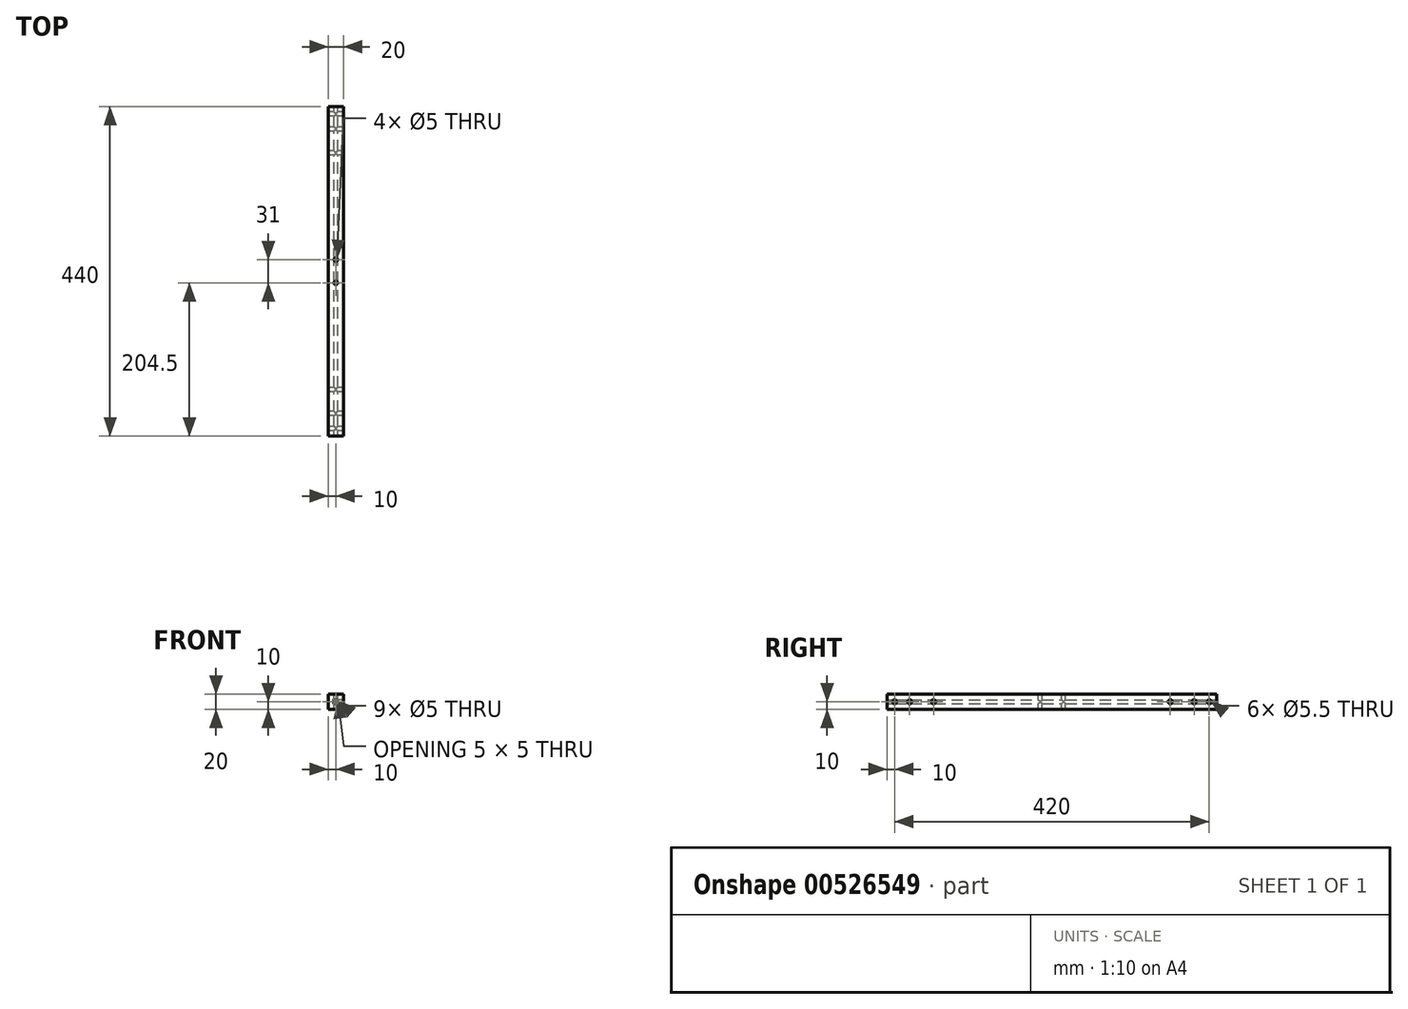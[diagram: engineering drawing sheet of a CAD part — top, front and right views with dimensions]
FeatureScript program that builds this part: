
annotation { "Feature Type Name" : "Feature", "Feature Type Description" : "" }
export const myFeature = defineFeature(function(context is Context, id is Id, definition is map)
    precondition{}
    {
        {
            var Q0;
            Q0=qCreatedBy(makeId("Front.planeOp"),FACE);
            var sketch = newSketch(context, id + "F0", { "sketchPlane" : qUnion([Q0])});
            skLineSegment(sketch, "E0.bottom", {"start": v(-10, 10) * mm, "end": v(10, 10) * mm});
            skLineSegment(sketch, "E0.top", {"start": v(-10, -10) * mm, "end": v(10, -10) * mm});
            skLineSegment(sketch, "E0.left", {"start": v(-10, 10) * mm, "end": v(-10, -10) * mm});
            skLineSegment(sketch, "E0.right", {"start": v(10, 10) * mm, "end": v(10, -10) * mm});
            skPoint(sketch, "E0.middle", {"position": v(0, 0) * mm});
            skCircle(sketch, "E1", {"center": v(0, 0) * mm, "radius": 2.5 * mm});
            skSolve(sketch);
        }
        {
            var Q0;
            Q0 = qSketchRegion(id + "F0", true);
            extrude(context, id + "F1", {"entities" : qUnion([Q0]), "endBound" : BoundingType.SYMMETRIC, "depth" : 440 * mm, "offsetDistance" : 25 * mm});
        }
        {
            var Q0;
            Q0=makeQuery(id+"F1.opExtrude","SWEPT_FACE",FACE,{"disambiguationData":[OSD([sQuery(id+"F0.wireOp",EDGE,"E0.left")])]});
            var sketch = newSketch(context, id + "F2", { "sketchPlane" : qUnion([Q0])});
            skCircle(sketch, "E2", {"center": v(-190, 0) * mm, "radius": 2.75 * mm});
            skCircle(sketch, "E3", {"center": v(-158, 0) * mm, "radius": 2.75 * mm});
            skCircle(sketch, "E4.MirrorC", {"center": v(158, 0) * mm, "radius": 2.75 * mm});
            skCircle(sketch, "E5.MirrorC", {"center": v(190, 0) * mm, "radius": 2.75 * mm});
            skCircle(sketch, "E6", {"center": v(-210, 0) * mm, "radius": 2.75 * mm});
            skPoint(sketch, "E6.centerSnap0", {"position": v(-220, 0) * mm});
            skCircle(sketch, "E7.MirrorC", {"center": v(210, 0) * mm, "radius": 2.75 * mm});
            skSolve(sketch);
        }
        {
            var Q0;
            Q0 = qSketchRegion(id + "F2", true);
            extrude(context, id + "F3", {"entities" : qUnion([Q0]), "operationType" : NewBodyOperationType.REMOVE, "oppositeDirection" : true, "depth" : 20 * mm, "offsetDistance" : 25 * mm});
        }
        {
            var Q0;
            Q0=qCreatedBy(makeId("Top.planeOp"),FACE);
            var sketch = newSketch(context, id + "F4", { "sketchPlane" : qUnion([Q0])});
            skCircle(sketch, "E8", {"center": v(0, 15.5) * mm, "radius": 2.5 * mm});
            skCircle(sketch, "E9.MirrorC", {"center": v(0, -15.5) * mm, "radius": 2.5 * mm});
            skSolve(sketch);
        }
        {
            var Q0;
            Q0 = qSketchRegion(id + "F4", true);
            extrude(context, id + "F5", {"entities" : qUnion([Q0]), "operationType" : NewBodyOperationType.REMOVE, "endBound" : BoundingType.SYMMETRIC, "oppositeDirection" : true, "depth" : 20 * mm, "offsetDistance" : 25 * mm});
        }
    });
